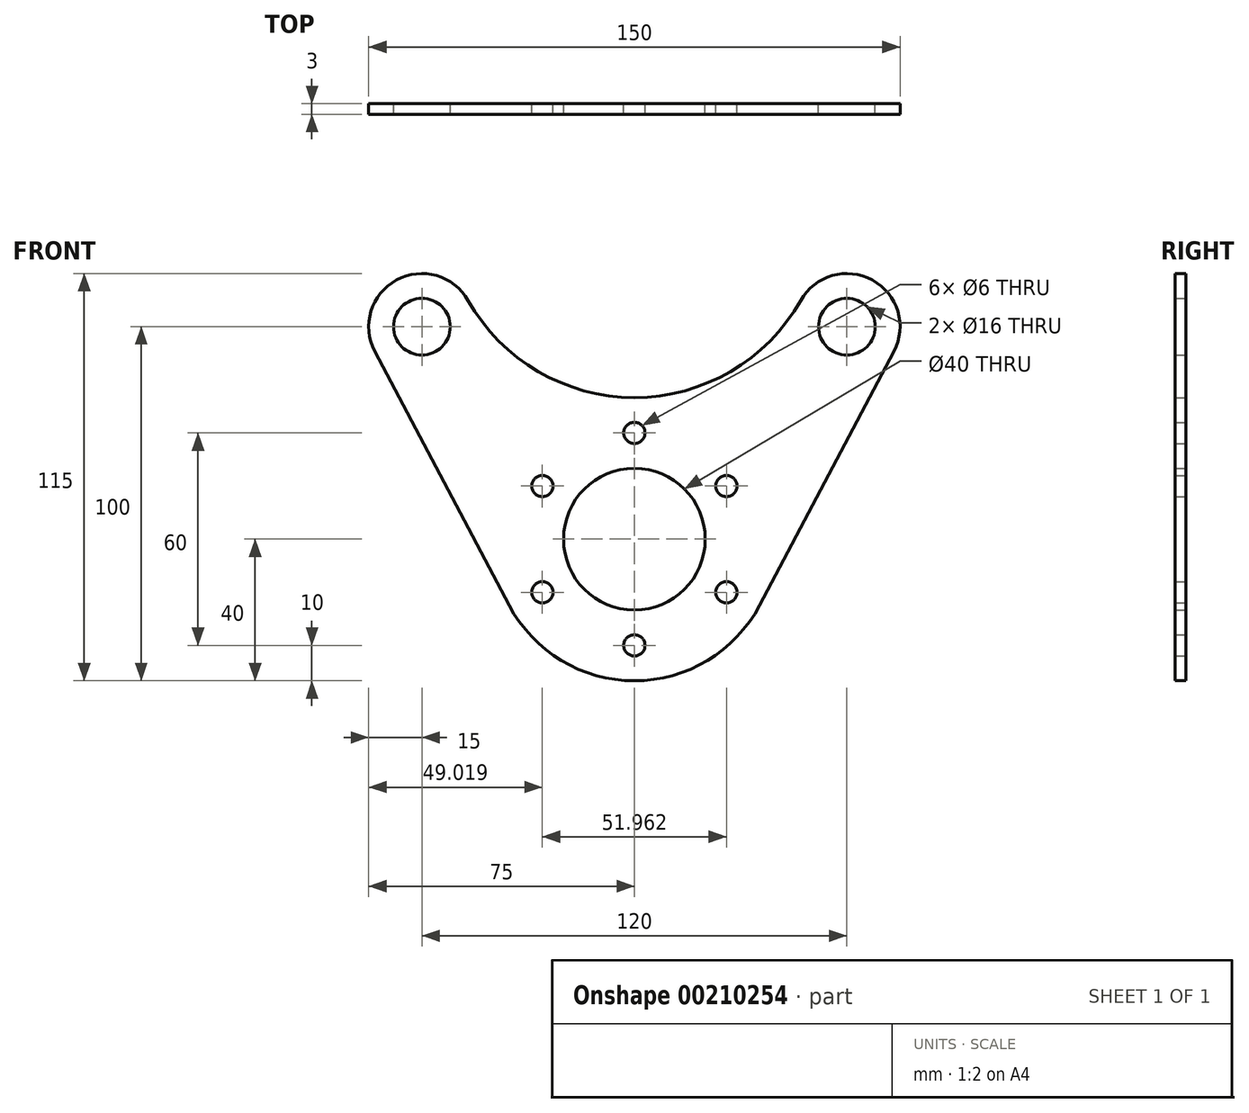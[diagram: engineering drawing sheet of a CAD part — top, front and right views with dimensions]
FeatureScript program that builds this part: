
annotation { "Feature Type Name" : "Feature", "Feature Type Description" : "" }
export const myFeature = defineFeature(function(context is Context, id is Id, definition is map)
    precondition{}
    {
        {
            var Q0;
            Q0=qCreatedBy(makeId("Front.planeOp"),FACE);
            var sketch = newSketch(context, id + "F0", { "sketchPlane" : qUnion([Q0])});
            skCircle(sketch, "E0", {"center": v(0, 0) * mm, "radius": 40 * mm});
            skCircle(sketch, "E1", {"center": v(-60, 60) * mm, "radius": 15 * mm});
            skCircle(sketch, "E2", {"center": v(60, 60) * mm, "radius": 15 * mm});
            skCircle(sketch, "E3", {"center": v(-60, 60) * mm, "radius": 8 * mm});
            skCircle(sketch, "E4", {"center": v(60, 60) * mm, "radius": 8 * mm});
            skLineSegment(sketch, "E5", {"start": v(-73.26, 52.99) * mm, "end": v(-35.36, -18.7) * mm});
            skLineSegment(sketch, "E6", {"start": v(73.26, 52.99) * mm, "end": v(35.36, -18.7) * mm});
            skArc(sketch, "E7", {"start": v(-46.94, 67.38) * mm, "mid": v(-27.17, 47.35) * mm, "end": v(0, 40) * mm});
            skArc(sketch, "E8", {"start": v(0, 40) * mm, "mid": v(27.17, 47.35) * mm, "end": v(46.94, 67.38) * mm});
            skCircle(sketch, "E9", {"center": v(0, 0) * mm, "radius": 20 * mm});
            skCircle(sketch, "E10", {"center": v(0, 30) * mm, "radius": 3 * mm});
            skCircle(sketch, "E11.1.0", {"center": v(-25.98, 15) * mm, "radius": 3 * mm});
            skCircle(sketch, "E11.2.0", {"center": v(-25.98, -15) * mm, "radius": 3 * mm});
            skCircle(sketch, "E11.3.0", {"center": v(0, -30) * mm, "radius": 3 * mm});
            skCircle(sketch, "E11.4.0", {"center": v(25.98, -15) * mm, "radius": 3 * mm});
            skCircle(sketch, "E11.5.0", {"center": v(25.98, 15) * mm, "radius": 3 * mm});
            skSolve(sketch);
        }
        {
            var Q0;
            Q0=makeQuery(id+"F0.imprint","IMPRINT",FACE,{"disambiguationData":[TD([[makeQuery(id+"F0.imprint","IMPRINT",EDGE,{"derivedFrom":sQuery(id+"F0.wireOp",EDGE,"E3")}),-1.0]])]});
            var Q1;
            Q1=makeQuery(id+"F0.imprint","IMPRINT",FACE,{"disambiguationData":[TD([[makeQuery(id+"F0.imprint","IMPRINT",EDGE,{"derivedFrom":sQuery(id+"F0.wireOp",EDGE,"E4")}),-1.0]])]});
            var Q2;
            Q2=makeQuery(id+"F0.imprint","IMPRINT",FACE,{"disambiguationData":[TD([[makeQuery(id+"F0.imprint","IMPRINT",EDGE,{"derivedFrom":sQuery(id+"F0.wireOp",EDGE,"E9")}),-1.0]])]});
            var Q3;
            {var subQ0=sQuery(id+"F0.wireOp",EDGE,"E6");Q3=makeQuery(id+"F0.imprint","IMPRINT",FACE,{"disambiguationData":[TD([[makeQuery(id+"F0.imprint","IMPRINT",EDGE,{"derivedFrom":subQ0}),-1.0]])]});}
            var Q4;
            {var subQ0=sQuery(id+"F0.wireOp",EDGE,"E5");Q4=makeQuery(id+"F0.imprint","IMPRINT",FACE,{"disambiguationData":[TD([[makeQuery(id+"F0.imprint","IMPRINT",EDGE,{"derivedFrom":subQ0}),1.0]])]});}
            extrude(context, id + "F1", {"entities" : qUnion([Q0, Q1, Q2, Q3, Q4]), "depth" : 3 * mm});
        }
    });
